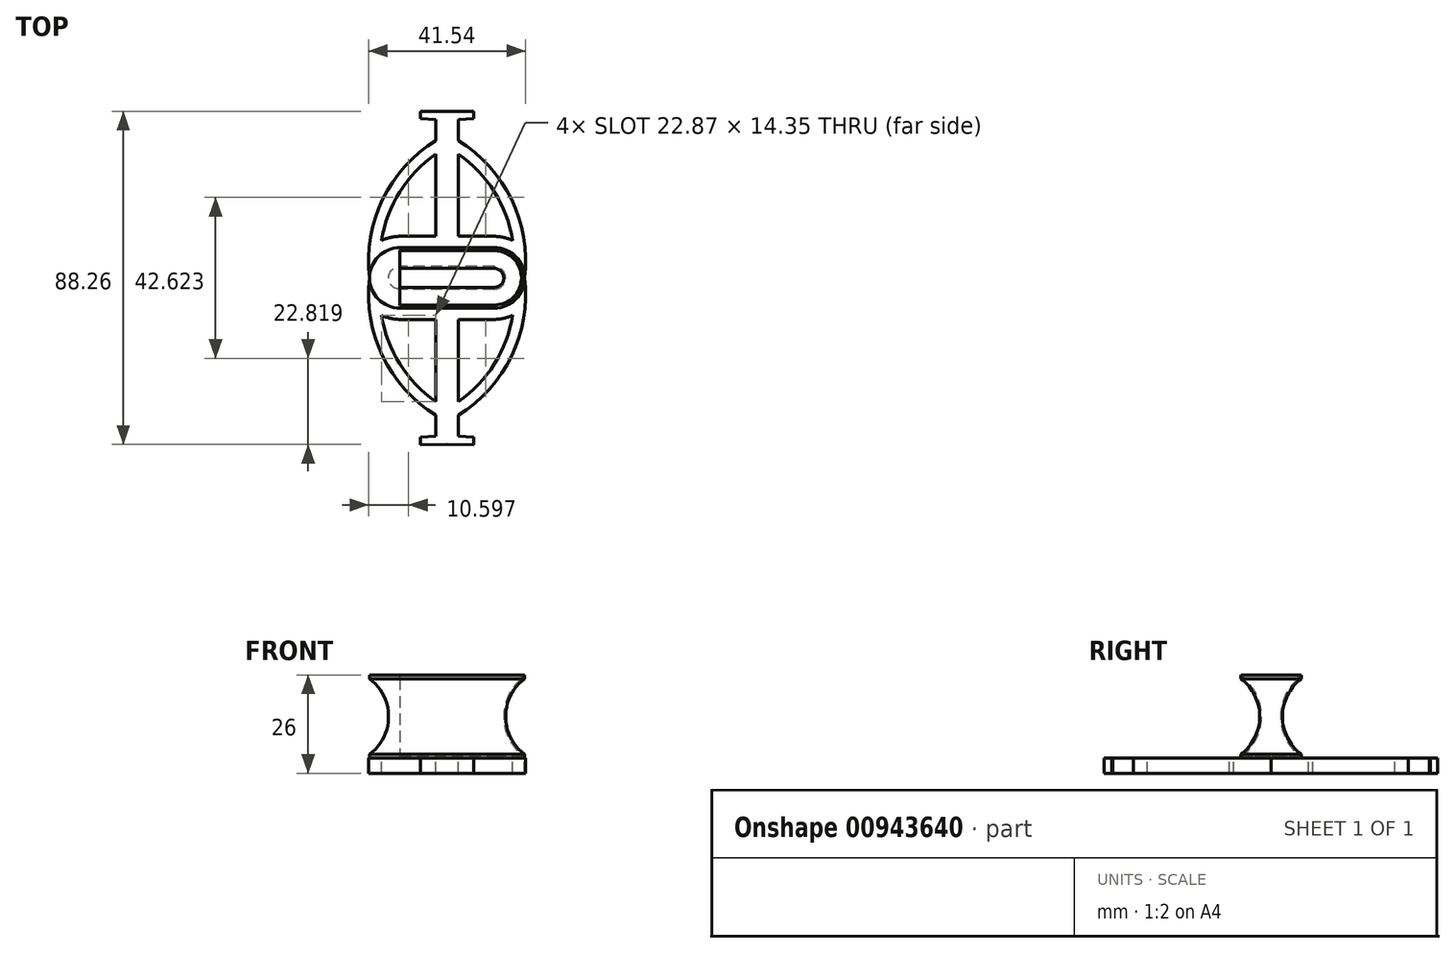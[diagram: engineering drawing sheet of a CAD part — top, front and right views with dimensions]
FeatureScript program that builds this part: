
annotation { "Feature Type Name" : "Feature", "Feature Type Description" : "" }
export const myFeature = defineFeature(function(context is Context, id is Id, definition is map)
    precondition{}
    {
        {
            var Q0;
            Q0=qCreatedBy(makeId("Right.planeOp"),FACE);
            var sketch = newSketch(context, id + "F0", { "sketchPlane" : qUnion([Q0])});
            skLineSegment(sketch, "E0", {"start": v(3, 0) * mm, "end": v(8, 0) * mm});
            skLineSegment(sketch, "E1", {"start": v(-3, 0) * mm, "end": v(-8, 0) * mm});
            skLineSegment(sketch, "E2", {"start": v(8, 0) * mm, "end": v(3, 0) * mm});
            skLineSegment(sketch, "E3", {"start": v(-8, 0) * mm, "end": v(-3, 0) * mm});
            skLineSegment(sketch, "E4", {"start": v(0, 10) * mm, "end": v(8, 10) * mm});
            skLineSegment(sketch, "E5.MirrorCS", {"start": v(0, -10) * mm, "end": v(8, -10) * mm});
            skArc(sketch, "E6", {"start": v(8, 10) * mm, "mid": v(3, 0) * mm, "end": v(8, -10) * mm});
            skArc(sketch, "E7.MirrorCS", {"start": v(-8, 10) * mm, "mid": v(-3, 0) * mm, "end": v(-8, -10) * mm});
            skLineSegment(sketch, "E8.MirrorCS", {"start": v(0, 10) * mm, "end": v(-8, 10) * mm});
            skLineSegment(sketch, "E9.MirrorCS", {"start": v(0, -10) * mm, "end": v(-8, -10) * mm});
            skPoint(sketch, "E10.end.orphan", {"position": v(3, 10) * mm});
            skPoint(sketch, "E11.MirrorCS.end.orphan", {"position": v(3, -10) * mm});
            skPoint(sketch, "E11.MirrorCS.start.orphan", {"position": v(3, 0) * mm});
            skPoint(sketch, "E12.MirrorCS.end.orphan", {"position": v(0, -10) * mm});
            skPoint(sketch, "E12.MirrorCS.start.orphan", {"position": v(0, 0) * mm});
            skPoint(sketch, "E13.MirrorCS.end.orphan", {"position": v(8, 0) * mm});
            skPoint(sketch, "E13.MirrorCS.start.orphan", {"position": v(8, -10) * mm});
            skSolve(sketch);
        }
        {
            var Q0;
            {var subQ3=sQuery(id+"F0.wireOp",EDGE,"E4");Q0=makeQuery(id+"F0.imprint","IMPRINT",FACE,{"disambiguationData":[TD([[makeQuery(id+"F0.imprint","IMPRINT",EDGE,{"derivedFrom":subQ3}),-1.0]])]});}
            extrude(context, id + "F1", {"entities" : qUnion([Q0]), "depth" : 25 * mm, "offsetDistance" : 25 * mm});
        }
        {
            var Q0;
            Q0=makeQuery(id+"F1.opExtrude","SWEPT_FACE",FACE,{"disambiguationData":[OSD([sQuery(id+"F0.wireOp",EDGE,"E4"),sQuery(id+"F0.wireOp",EDGE,"E8.MirrorCS")])]});
            extrude(context, id + "F2", {"entities" : qUnion([Q0]), "operationType" : NewBodyOperationType.ADD, "depth" : 1 * mm, "offsetDistance" : 25 * mm});
        }
        {
            var Q0;
            Q0=makeQuery(id+"F1.opExtrude","SWEPT_FACE",FACE,{"disambiguationData":[OSD([sQuery(id+"F0.wireOp",EDGE,"E5.MirrorCS"),sQuery(id+"F0.wireOp",EDGE,"E9.MirrorCS")])]});
            extrude(context, id + "F3", {"entities" : qUnion([Q0]), "operationType" : NewBodyOperationType.ADD, "depth" : 1 * mm, "offsetDistance" : 25 * mm});
        }
        {
            var Q0;
            {var subQ0=sQuery(id+"F0.wireOp",EDGE,"E9.MirrorCS");var subQ1=sQuery(id+"F0.wireOp",EDGE,"E5.MirrorCS");var subQ2=sQuery(id+"F0.wireOp",EDGE,"E8.MirrorCS");var subQ3=sQuery(id+"F0.wireOp",EDGE,"E4");Q0=makeQuery(id+"F3.boolean.opBoolean","MERGE",FACE,{"derivedFrom":[makeQuery(id+"F2.boolean.opBoolean","MERGE",FACE,{"derivedFrom":[makeQuery(id+"F1.opExtrude","CAP_FACE",FACE,{"disambiguationData":[OSD([subQ3,subQ1,sQuery(id+"F0.wireOp",EDGE,"E6"),sQuery(id+"F0.wireOp",EDGE,"E7.MirrorCS"),subQ2,subQ0])],"isStart":true}),makeQuery(id+"F2.opExtrude","SWEPT_FACE",FACE,{"disambiguationData":[OSD([subQ3,subQ2]),TDD([makeQuery(id+"F1.opExtrude","CAP_EDGE",EDGE,{"disambiguationData":[OSD([subQ3,subQ2])],"isStart":true})])]})]}),makeQuery(id+"F3.opExtrude","SWEPT_FACE",FACE,{"disambiguationData":[OSD([subQ1,subQ0]),TDD([makeQuery(id+"F1.opExtrude","CAP_EDGE",EDGE,{"disambiguationData":[OSD([subQ1,subQ0])],"isStart":true})])]})]});}
            var sketch = newSketch(context, id + "F4", { "sketchPlane" : qUnion([Q0])});
            skLineSegment(sketch, "E14", {"start": v(0, 11) * mm, "end": v(0, -11) * mm});
            skSolve(sketch);
        }
        {
            var Q0;
            {var subQ5=sQuery(id+"F4.wireOp",EDGE,"E14");Q0=makeQuery(id+"F4.imprint","IMPRINT",FACE,{"disambiguationData":[TD([[makeQuery(id+"F4.imprint","IMPRINT",EDGE,{"derivedFrom":subQ5}),-1.0]])]});}
            var Q1;
            Q1=sQuery(id+"F4.wireOp",EDGE,"E14");
            revolve(context, id + "F5", {"operationType" : NewBodyOperationType.ADD, "surfaceOperationType" : NewSurfaceOperationType.NEW, "entities" : qUnion([Q0]), "axis" : qUnion([Q1]), "revolveType" : RevolveType.FULL});
        }
        {
            var Q0;
            {var subQ0=sQuery(id+"F0.wireOp",EDGE,"E9.MirrorCS");var subQ1=sQuery(id+"F0.wireOp",EDGE,"E5.MirrorCS");var subQ2=sQuery(id+"F0.wireOp",EDGE,"E8.MirrorCS");var subQ3=sQuery(id+"F0.wireOp",EDGE,"E4");Q0=makeQuery(id+"F3.boolean.opBoolean","MERGE",FACE,{"derivedFrom":[makeQuery(id+"F2.boolean.opBoolean","MERGE",FACE,{"derivedFrom":[makeQuery(id+"F1.opExtrude","CAP_FACE",FACE,{"disambiguationData":[OSD([subQ3,subQ1,sQuery(id+"F0.wireOp",EDGE,"E6"),sQuery(id+"F0.wireOp",EDGE,"E7.MirrorCS"),subQ2,subQ0])],"isStart":false}),makeQuery(id+"F2.opExtrude","SWEPT_FACE",FACE,{"disambiguationData":[OSD([subQ3,subQ2]),TDD([makeQuery(id+"F1.opExtrude","CAP_EDGE",EDGE,{"disambiguationData":[OSD([subQ3,subQ2])],"isStart":false})])]})]}),makeQuery(id+"F3.opExtrude","SWEPT_FACE",FACE,{"disambiguationData":[OSD([subQ1,subQ0]),TDD([makeQuery(id+"F1.opExtrude","CAP_EDGE",EDGE,{"disambiguationData":[OSD([subQ1,subQ0])],"isStart":false})])]})]});}
            var sketch = newSketch(context, id + "F6", { "sketchPlane" : qUnion([Q0])});
            skArc(sketch, "E15.0", {"start": v(7.84, -10.5) * mm, "mid": v(2.5, 0) * mm, "end": v(7.84, 10.5) * mm});
            skLineSegment(sketch, "E15.1", {"start": v(-7.84, -10.5) * mm, "end": v(7.84, -10.5) * mm});
            skArc(sketch, "E15.2", {"start": v(-7.2, 10) * mm, "mid": v(-2.5, -0.4) * mm, "end": v(-7.84, -10.5) * mm});
            skLineSegment(sketch, "E15.3", {"start": v(7.84, 10.5) * mm, "end": v(7.2, 10.5) * mm});
            skLineSegment(sketch, "E16", {"start": v(-7.2, 10) * mm, "end": v(-7.2, 11) * mm});
            skLineSegment(sketch, "E17.MirrorCS", {"start": v(7.2, 10) * mm, "end": v(7.2, 11) * mm});
            skLineSegment(sketch, "E18", {"start": v(-7.2, 11) * mm, "end": v(7.2, 11) * mm});
            skSolve(sketch);
        }
        {
            var Q0;
            {var subQ0=sQuery(id+"F6.wireOp",EDGE,"E15.1");Q0=makeQuery(id+"F6.imprint","IMPRINT",FACE,{"disambiguationData":[TD([[makeQuery(id+"F6.imprint","IMPRINT",EDGE,{"derivedFrom":subQ0}),1.0]])]});}
            extrude(context, id + "F7", {"entities" : qUnion([Q0]), "operationType" : NewBodyOperationType.REMOVE, "oppositeDirection" : true, "depth" : 25 * mm, "offsetDistance" : 25 * mm});
        }
        {
            var Q0;
            {var subQ0=sQuery(id+"F0.wireOp",EDGE,"E9.MirrorCS");var subQ1=sQuery(id+"F0.wireOp",EDGE,"E5.MirrorCS");var subQ2=sQuery(id+"F0.wireOp",EDGE,"E8.MirrorCS");var subQ3=sQuery(id+"F0.wireOp",EDGE,"E4");Q0=makeQuery(id+"F3.boolean.opBoolean","MERGE",FACE,{"derivedFrom":[makeQuery(id+"F2.boolean.opBoolean","MERGE",FACE,{"derivedFrom":[makeQuery(id+"F1.opExtrude","CAP_FACE",FACE,{"disambiguationData":[OSD([subQ3,subQ1,sQuery(id+"F0.wireOp",EDGE,"E6"),sQuery(id+"F0.wireOp",EDGE,"E7.MirrorCS"),subQ2,subQ0])],"isStart":false}),makeQuery(id+"F2.opExtrude","SWEPT_FACE",FACE,{"disambiguationData":[OSD([subQ3,subQ2]),TDD([makeQuery(id+"F1.opExtrude","CAP_EDGE",EDGE,{"disambiguationData":[OSD([subQ3,subQ2])],"isStart":false})])]})]}),makeQuery(id+"F3.opExtrude","SWEPT_FACE",FACE,{"disambiguationData":[OSD([subQ1,subQ0]),TDD([makeQuery(id+"F1.opExtrude","CAP_EDGE",EDGE,{"disambiguationData":[OSD([subQ1,subQ0])],"isStart":false})])]})]});}
            var sketch = newSketch(context, id + "F8", { "sketchPlane" : qUnion([Q0])});
            skLineSegment(sketch, "E19.0", {"start": v(-7.2, 11) * mm, "end": v(7.2, 11) * mm});
            skPoint(sketch, "E20.0", {"position": v(8, 11) * mm});
            skPoint(sketch, "E21.0", {"position": v(8, 10.5) * mm});
            skLineSegment(sketch, "E22.0", {"start": v(8, 11) * mm, "end": v(8, 10) * mm});
            skLineSegment(sketch, "E23.0", {"start": v(7.2, 11) * mm, "end": v(8, 11) * mm});
            skArc(sketch, "E24.0", {"start": v(8, 10) * mm, "mid": v(3, 0) * mm, "end": v(8, -10) * mm});
            skLineSegment(sketch, "E25.0", {"start": v(-8, 11) * mm, "end": v(-7.2, 11) * mm});
            skLineSegment(sketch, "E26.0", {"start": v(-8, 11) * mm, "end": v(-8, 10) * mm});
            skArc(sketch, "E27.0", {"start": v(-8, 10) * mm, "mid": v(-3, 0) * mm, "end": v(-8, -10) * mm});
            skLineSegment(sketch, "E28.0", {"start": v(-8, -11) * mm, "end": v(-8, -10) * mm});
            skLineSegment(sketch, "E29.0", {"start": v(8, -11) * mm, "end": v(-8, -11) * mm});
            skLineSegment(sketch, "E30.0", {"start": v(8, -11) * mm, "end": v(8, -10) * mm});
            skLineSegment(sketch, "E31", {"start": v(0, 11) * mm, "end": v(0, -11) * mm});
            skSolve(sketch);
        }
        {
            var Q0;
            Q0=makeQuery(id+"F8.imprint","IMPRINT",FACE,{"disambiguationData":[TD([[makeQuery(id+"F8.imprint","IMPRINT",EDGE,{"derivedFrom":sQuery(id+"F8.wireOp",EDGE,"E25.0")}),-1.0]])]});
            var Q1;
            {var subQ6=makeQuery(id+"F7.boolean.opBoolean","COPY",EDGE,{"derivedFrom":makeQuery(id+"F7.opExtrude","CAP_EDGE",EDGE,{"disambiguationData":[OSD([sQuery(id+"F6.wireOp",EDGE,"E15.2")])],"isStart":true})});Q1=makeQuery(id+"F8.imprint","IMPRINT",FACE,{"disambiguationData":[TD([[makeQuery(id+"F8.imprint","IMPRINT",EDGE,{"derivedFrom":subQ6}),1.0]])]});}
            var Q2;
            Q2=sQuery(id+"F8.wireOp",EDGE,"E31");
            revolve(context, id + "F9", {"operationType" : NewBodyOperationType.ADD, "surfaceOperationType" : NewSurfaceOperationType.NEW, "entities" : qUnion([Q0, Q1]), "axis" : qUnion([Q2]), "revolveType" : RevolveType.ONE_DIRECTION, "oppositeDirection" : true, "angle" : 180 * degree});
        }
        {
            var Q0;
            {var subQ0=sQuery(id+"F0.wireOp",EDGE,"E9.MirrorCS");var subQ1=sQuery(id+"F0.wireOp",EDGE,"E5.MirrorCS");Q0=makeQuery(id+"F9.boolean.opBoolean","MERGE",FACE,{"derivedFrom":[makeQuery(id+"F5.boolean.opBoolean","MERGE",FACE,{"derivedFrom":[makeQuery(id+"F3.opExtrude","CAP_FACE",FACE,{"disambiguationData":[OSD([subQ1,subQ0])],"isStart":false}),makeQuery(id+"F5.opRevolve","SWEPT_FACE",FACE,{"disambiguationData":[OSD([subQ1,subQ0])]})]}),makeQuery(id+"F9.opRevolve","SWEPT_FACE",FACE,{"disambiguationData":[OSD([sQuery(id+"F8.wireOp",EDGE,"E29.0")])]})]});}
            var sketch = newSketch(context, id + "F10", { "sketchPlane" : qUnion([Q0])});
            skArc(sketch, "E32", {"start": v(9.57, 36.38) * mm, "mid": v(-4.54, 20.76) * mm, "end": v(-8, 0) * mm});
            skLineSegment(sketch, "E33", {"start": v(9.57, 38) * mm, "end": v(9.57, 36.38) * mm});
            skLineSegment(sketch, "E34", {"start": v(9.57, 36.38) * mm, "end": v(9.57, 41.88) * mm});
            skLineSegment(sketch, "E35", {"start": v(9.57, 41.88) * mm, "end": v(5.44, 42.2) * mm});
            skLineSegment(sketch, "E36", {"start": v(5.44, 42.2) * mm, "end": v(5.44, 44.13) * mm});
            skLineSegment(sketch, "E37", {"start": v(5.44, 44.13) * mm, "end": v(12.5, 44.1) * mm});
            skLineSegment(sketch, "E38", {"start": v(12.5, 44.1) * mm, "end": v(12.5, 38) * mm});
            skLineSegment(sketch, "E39.0.0", {"start": v(25, 8) * mm, "end": v(12.5, 8) * mm});
            skArc(sketch, "E39.0.1", {"start": v(0, 8) * mm, "mid": v(-5.66, 5.66) * mm, "end": v(-8, 0) * mm});
            skLineSegment(sketch, "E39.0.2", {"start": v(0, -8) * mm, "end": v(25, -8) * mm});
            skArc(sketch, "E39.0.3", {"start": v(25, -8) * mm, "mid": v(33, 0) * mm, "end": v(25, 8) * mm});
            skLineSegment(sketch, "E40", {"start": v(12.5, 8) * mm, "end": v(0, 8) * mm});
            skArc(sketch, "E41", {"start": v(-8, 0) * mm, "mid": v(-5.66, -5.66) * mm, "end": v(0, -8) * mm});
            skArc(sketch, "E42.0", {"start": v(0, 11) * mm, "mid": v(-2.49, 10.72) * mm, "end": v(-4.85, 9.88) * mm});
            skLineSegment(sketch, "E42.1", {"start": v(9.5, 11) * mm, "end": v(0, 11) * mm});
            skLineSegment(sketch, "E42.2", {"start": v(9.5, 11) * mm, "end": v(9.5, 32.75) * mm});
            skArc(sketch, "E42.3", {"start": v(9.5, 32.75) * mm, "mid": v(0, 22.78) * mm, "end": v(-4.85, 9.88) * mm});
            skLineSegment(sketch, "E43.MirrorCS", {"start": v(15.43, 36.38) * mm, "end": v(15.43, 41.88) * mm});
            skLineSegment(sketch, "E44.MirrorCS", {"start": v(15.43, 41.88) * mm, "end": v(19.56, 42.2) * mm});
            skLineSegment(sketch, "E45.MirrorCS", {"start": v(19.56, 44.13) * mm, "end": v(12.5, 44.1) * mm});
            skLineSegment(sketch, "E46.MirrorCS", {"start": v(19.56, 42.2) * mm, "end": v(19.56, 44.13) * mm});
            skArc(sketch, "E47.MirrorCS", {"start": v(15.43, 36.38) * mm, "mid": v(29.54, 20.76) * mm, "end": v(33, 0) * mm});
            skLineSegment(sketch, "E48.MirrorCS", {"start": v(15.5, 11) * mm, "end": v(25, 11) * mm});
            skArc(sketch, "E49.MirrorCS", {"start": v(25, 11) * mm, "mid": v(27.49, 10.72) * mm, "end": v(29.85, 9.88) * mm});
            skArc(sketch, "E50.MirrorCS", {"start": v(15.5, 32.75) * mm, "mid": v(25, 22.78) * mm, "end": v(29.85, 9.88) * mm});
            skLineSegment(sketch, "E51.MirrorCS", {"start": v(15.5, 11) * mm, "end": v(15.5, 32.75) * mm});
            skArc(sketch, "E52.MirrorCS", {"start": v(12.5, -38) * mm, "mid": v(-3.78, -22.25) * mm, "end": v(-8, 0) * mm});
            skArc(sketch, "E53.MirrorCS", {"start": v(15.43, -36.38) * mm, "mid": v(29.54, -20.76) * mm, "end": v(33, 0) * mm});
            skArc(sketch, "E54.MirrorCS", {"start": v(0, -11) * mm, "mid": v(-2.49, -10.72) * mm, "end": v(-4.85, -9.88) * mm});
            skLineSegment(sketch, "E55.MirrorCS", {"start": v(9.5, -11) * mm, "end": v(0, -11) * mm});
            skLineSegment(sketch, "E56.MirrorCS", {"start": v(15.5, -11) * mm, "end": v(25, -11) * mm});
            skArc(sketch, "E57.MirrorCS", {"start": v(25, -11) * mm, "mid": v(27.49, -10.72) * mm, "end": v(29.85, -9.88) * mm});
            skArc(sketch, "E58.MirrorCS", {"start": v(15.5, -32.75) * mm, "mid": v(25, -22.78) * mm, "end": v(29.85, -9.88) * mm});
            skLineSegment(sketch, "E59.MirrorCS", {"start": v(15.5, -11) * mm, "end": v(15.5, -32.75) * mm});
            skLineSegment(sketch, "E60.MirrorCS", {"start": v(9.5, -11) * mm, "end": v(9.5, -32.75) * mm});
            skArc(sketch, "E61.MirrorCS", {"start": v(9.5, -32.75) * mm, "mid": v(0, -22.78) * mm, "end": v(-4.85, -9.88) * mm});
            skLineSegment(sketch, "E62.MirrorCS", {"start": v(9.57, -36.38) * mm, "end": v(9.57, -41.88) * mm});
            skLineSegment(sketch, "E63.MirrorCS", {"start": v(15.43, -36.38) * mm, "end": v(15.43, -41.88) * mm});
            skLineSegment(sketch, "E64.MirrorCS", {"start": v(9.57, -41.88) * mm, "end": v(5.44, -42.2) * mm});
            skLineSegment(sketch, "E65.MirrorCS", {"start": v(5.44, -42.2) * mm, "end": v(5.44, -44.13) * mm});
            skLineSegment(sketch, "E66.MirrorCS", {"start": v(5.44, -44.13) * mm, "end": v(12.5, -44.1) * mm});
            skLineSegment(sketch, "E67.MirrorCS", {"start": v(19.56, -44.13) * mm, "end": v(12.5, -44.1) * mm});
            skLineSegment(sketch, "E68.MirrorCS", {"start": v(19.56, -42.2) * mm, "end": v(19.56, -44.13) * mm});
            skLineSegment(sketch, "E69.MirrorCS", {"start": v(15.43, -41.88) * mm, "end": v(19.56, -42.2) * mm});
            skPoint(sketch, "E70.orphan", {"position": v(12.5, 38) * mm});
            skPoint(sketch, "E71.start.orphan", {"position": v(12.5, 8) * mm});
            skPoint(sketch, "E72.orphan", {"position": v(12.5, -38) * mm});
            skSolve(sketch);
        }
        {
            var Q0;
            {var subQ3=sQuery(id+"F10.wireOp",EDGE,"E32");Q0=makeQuery(id+"F10.imprint","IMPRINT",FACE,{"disambiguationData":[TD([[makeQuery(id+"F10.imprint","IMPRINT",EDGE,{"derivedFrom":subQ3}),1.0]])]});}
            var Q1;
            {var subQ1=sQuery(id+"F10.wireOp",EDGE,"E39.0.2");Q1=makeQuery(id+"F10.imprint","IMPRINT",FACE,{"disambiguationData":[TD([[makeQuery(id+"F10.imprint","IMPRINT",EDGE,{"derivedFrom":subQ1}),1.0]])]});}
            var Q2;
            {var subQ3=sQuery(id+"F10.wireOp",EDGE,"E39.0.0");Q2=makeQuery(id+"F10.imprint","IMPRINT",FACE,{"disambiguationData":[TD([[makeQuery(id+"F10.imprint","IMPRINT",EDGE,{"derivedFrom":subQ3}),1.0]])]});}
            extrude(context, id + "F11", {"entities" : qUnion([Q0, Q1, Q2]), "operationType" : NewBodyOperationType.ADD, "depth" : 4 * mm, "offsetDistance" : 25 * mm});
        }
    });
